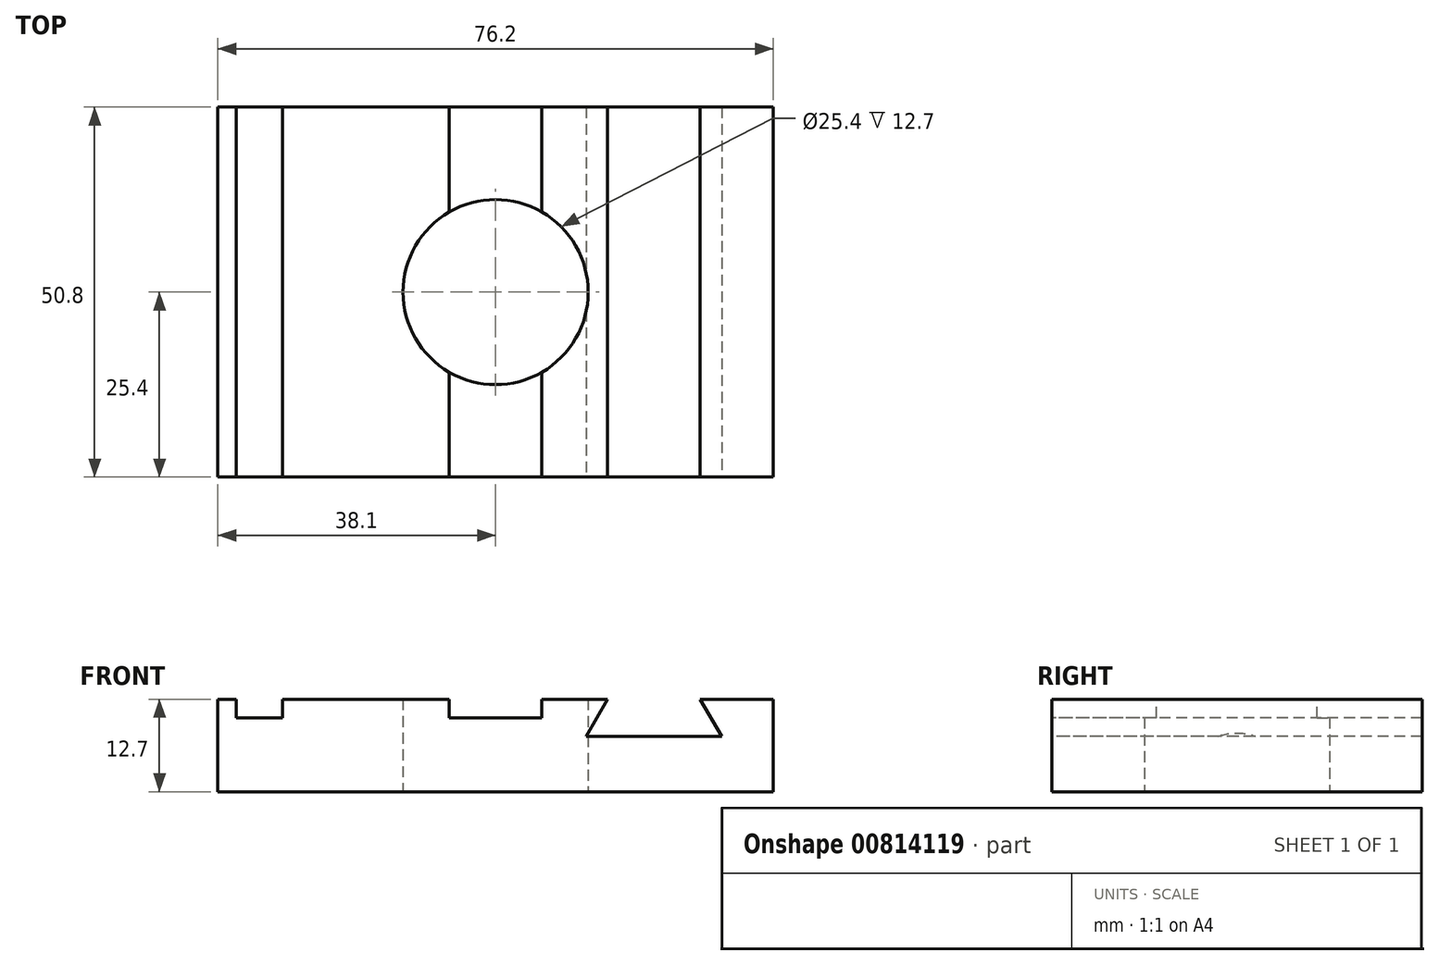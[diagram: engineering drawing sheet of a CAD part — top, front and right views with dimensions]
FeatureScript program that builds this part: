
annotation { "Feature Type Name" : "Feature", "Feature Type Description" : "" }
export const myFeature = defineFeature(function(context is Context, id is Id, definition is map)
    precondition{}
    {
        {
            var Q0;
            Q0=qCreatedBy(makeId("Top.planeOp"),FACE);
            var sketch = newSketch(context, id + "F0", { "sketchPlane" : qUnion([Q0])});
            skLineSegment(sketch, "E0.bottom", {"start": v(-38.1, 25.4) * mm, "end": v(38.1, 25.4) * mm});
            skLineSegment(sketch, "E0.top", {"start": v(-38.1, -25.4) * mm, "end": v(38.1, -25.4) * mm});
            skLineSegment(sketch, "E0.left", {"start": v(-38.1, 25.4) * mm, "end": v(-38.1, -25.4) * mm});
            skLineSegment(sketch, "E0.right", {"start": v(38.1, 25.4) * mm, "end": v(38.1, -25.4) * mm});
            skPoint(sketch, "E0.middle", {"position": v(0, 0) * mm});
            skCircle(sketch, "E1", {"center": v(0, 0) * mm, "radius": 12.7 * mm});
            skSolve(sketch);
        }
        {
            var Q0;
            Q0=makeQuery(id+"F0.imprint","IMPRINT",FACE,{"disambiguationData":[TD([[makeQuery(id+"F0.imprint","IMPRINT",EDGE,{"derivedFrom":sQuery(id+"F0.wireOp",EDGE,"E0.bottom")}),-1.0]])]});
            extrude(context, id + "F1", {"entities" : qUnion([Q0]), "depth" : 12.7 * mm, "offsetDistance" : 25.4 * mm});
        }
        {
            var Q0;
            Q0=makeQuery(id+"F1.opExtrude","CAP_FACE",FACE,{"disambiguationData":[OSD([sQuery(id+"F0.wireOp",EDGE,"E0.bottom"),sQuery(id+"F0.wireOp",EDGE,"E0.top"),sQuery(id+"F0.wireOp",EDGE,"E0.left"),sQuery(id+"F0.wireOp",EDGE,"E0.right"),sQuery(id+"F0.wireOp",EDGE,"E1")])],"isStart":false});
            var sketch = newSketch(context, id + "F2", { "sketchPlane" : qUnion([Q0])});
            skLineSegment(sketch, "E2.bottom", {"start": v(-35.56, 25.4) * mm, "end": v(-29.21, 25.4) * mm});
            skLineSegment(sketch, "E2.top", {"start": v(-35.56, -25.4) * mm, "end": v(-29.21, -25.4) * mm});
            skLineSegment(sketch, "E2.left", {"start": v(-35.56, 25.4) * mm, "end": v(-35.56, -25.4) * mm});
            skLineSegment(sketch, "E2.right", {"start": v(-29.21, 25.4) * mm, "end": v(-29.21, -25.4) * mm});
            skLineSegment(sketch, "E3", {"start": v(-6.35, 25.4) * mm, "end": v(-6.35, -25.4) * mm});
            skLineSegment(sketch, "E4", {"start": v(-6.35, -25.4) * mm, "end": v(6.35, -25.4) * mm});
            skLineSegment(sketch, "E5", {"start": v(6.35, -25.4) * mm, "end": v(6.35, 25.4) * mm});
            skLineSegment(sketch, "E6", {"start": v(6.35, 25.4) * mm, "end": v(-6.35, 25.4) * mm});
            skPoint(sketch, "E7", {"position": v(0, 0) * mm});
            skLineSegment(sketch, "E8", {"start": v(0, 25.4) * mm, "end": v(0, -25.4) * mm, "construction": true});
            skSolve(sketch);
        }
        {
            var Q0;
            Q0=makeQuery(id+"F2.imprint","IMPRINT",FACE,{"disambiguationData":[TD([[makeQuery(id+"F2.imprint","IMPRINT",EDGE,{"derivedFrom":sQuery(id+"F2.wireOp",EDGE,"E2.bottom")}),-1.0]])]});
            var Q1;
            {var subQ0=sQuery(id+"F2.wireOp",EDGE,"E4");Q1=makeQuery(id+"F2.imprint","IMPRINT",FACE,{"disambiguationData":[TD([[makeQuery(id+"F2.imprint","IMPRINT",EDGE,{"derivedFrom":subQ0}),1.0]])]});}
            var Q2;
            {var subQ0=sQuery(id+"F2.wireOp",EDGE,"E6");Q2=makeQuery(id+"F2.imprint","IMPRINT",FACE,{"disambiguationData":[TD([[makeQuery(id+"F2.imprint","IMPRINT",EDGE,{"derivedFrom":subQ0}),-1.0]])]});}
            extrude(context, id + "F3", {"entities" : qUnion([Q0, Q1, Q2]), "operationType" : NewBodyOperationType.REMOVE, "oppositeDirection" : true, "depth" : 2.54 * mm, "offsetDistance" : 25.4 * mm});
        }
        {
            var Q0;
            Q0=makeQuery(id+"F1.opExtrude","SWEPT_FACE",FACE,{"disambiguationData":[OSD([sQuery(id+"F0.wireOp",EDGE,"E0.top")])]});
            var sketch = newSketch(context, id + "F4", { "sketchPlane" : qUnion([Q0])});
            skLineSegment(sketch, "E9", {"start": v(15.37, 12.7) * mm, "end": v(12.44, 7.62) * mm});
            skLineSegment(sketch, "E10", {"start": v(12.44, 7.62) * mm, "end": v(31, 7.62) * mm});
            skLineSegment(sketch, "E11", {"start": v(31, 7.62) * mm, "end": v(28.07, 12.7) * mm});
            skLineSegment(sketch, "E12", {"start": v(25.4, 12.7) * mm, "end": v(25.4, 7.62) * mm, "construction": true});
            skSolve(sketch);
        }
        {
            var Q0;
            {var subQ0=sQuery(id+"F4.wireOp",EDGE,"E9");Q0=makeQuery(id+"F4.imprint","IMPRINT",FACE,{"disambiguationData":[TD([[makeQuery(id+"F4.imprint","IMPRINT",EDGE,{"derivedFrom":subQ0}),1.0]])]});}
            extrude(context, id + "F5", {"entities" : qUnion([Q0]), "operationType" : NewBodyOperationType.REMOVE, "endBound" : BoundingType.THROUGH_ALL, "oppositeDirection" : true, "depth" : 25.4 * mm, "offsetDistance" : 25.4 * mm});
        }
    });
